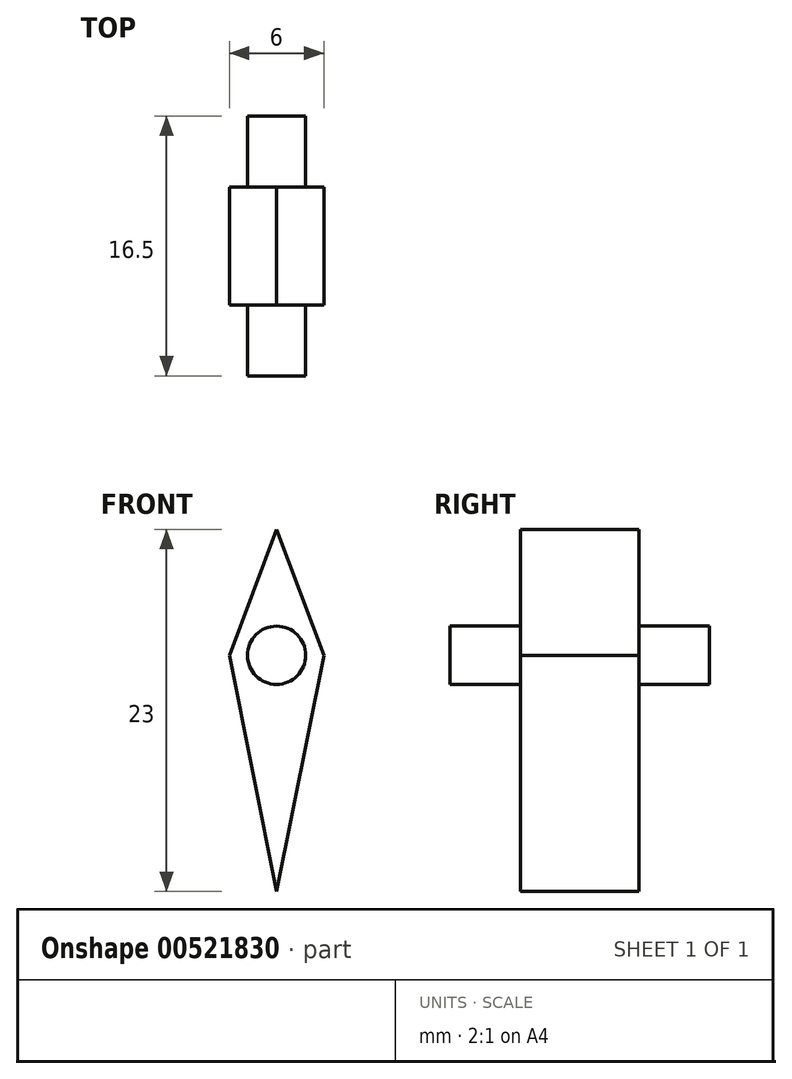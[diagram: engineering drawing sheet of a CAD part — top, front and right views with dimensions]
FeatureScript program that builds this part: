
annotation { "Feature Type Name" : "Feature", "Feature Type Description" : "" }
export const myFeature = defineFeature(function(context is Context, id is Id, definition is map)
    precondition{}
    {
        {
            var Q0;
            Q0=qCreatedBy(makeId("Front.planeOp"),FACE);
            var sketch = newSketch(context, id + "F0", { "sketchPlane" : qUnion([Q0])});
            skCircle(sketch, "E0", {"center": v(0, 0) * mm, "radius": 1.85 * mm});
            skLineSegment(sketch, "E1", {"start": v(0, 0) * mm, "end": v(0, 8) * mm});
            skLineSegment(sketch, "E2", {"start": v(0, 0) * mm, "end": v(0, -15) * mm});
            skLineSegment(sketch, "E3", {"start": v(0, 0) * mm, "end": v(-3, 0) * mm});
            skLineSegment(sketch, "E4", {"start": v(0, 0) * mm, "end": v(3, 0) * mm});
            skLineSegment(sketch, "E5", {"start": v(3, 0) * mm, "end": v(0, 8) * mm});
            skLineSegment(sketch, "E6", {"start": v(0, 8) * mm, "end": v(-3, 0) * mm});
            skLineSegment(sketch, "E7", {"start": v(0, -15) * mm, "end": v(-3, 0) * mm});
            skLineSegment(sketch, "E8", {"start": v(0, -15) * mm, "end": v(3, 0) * mm});
            skSolve(sketch);
        }
        {
            var Q0;
            {var subQ5=sQuery(id+"F0.wireOp",EDGE,"E8");Q0=makeQuery(id+"F0.imprint","IMPRINT",FACE,{"disambiguationData":[TD([[makeQuery(id+"F0.imprint","IMPRINT",EDGE,{"derivedFrom":subQ5}),1.0]])]});}
            var Q1;
            {var subQ5=sQuery(id+"F0.wireOp",EDGE,"E7");Q1=makeQuery(id+"F0.imprint","IMPRINT",FACE,{"disambiguationData":[TD([[makeQuery(id+"F0.imprint","IMPRINT",EDGE,{"derivedFrom":subQ5}),-1.0]])]});}
            var Q2;
            {var subQ0=sQuery(id+"F0.wireOp",EDGE,"E3");var subQ1=sQuery(id+"F0.wireOp",EDGE,"E0");var subQ2=makeQuery(id+"F0.imprint","INTERSECT",VERTEX,{"derivedFrom":[subQ1,subQ0]});Q2=makeQuery(id+"F0.imprint","IMPRINT",FACE,{"disambiguationData":[TD([[makeQuery(id+"F0.imprint","IMPRINT",EDGE,{"disambiguationData":[TD([[subQ2,-1.0]])],"derivedFrom":subQ1}),1.0]])]});}
            var Q3;
            {var subQ0=sQuery(id+"F0.wireOp",EDGE,"E2");var subQ1=sQuery(id+"F0.wireOp",EDGE,"E0");var subQ2=makeQuery(id+"F0.imprint","INTERSECT",VERTEX,{"derivedFrom":[subQ1,subQ0]});Q3=makeQuery(id+"F0.imprint","IMPRINT",FACE,{"disambiguationData":[TD([[makeQuery(id+"F0.imprint","IMPRINT",EDGE,{"disambiguationData":[TD([[subQ2,-1.0]])],"derivedFrom":subQ1}),1.0]])]});}
            var Q4;
            {var subQ0=sQuery(id+"F0.wireOp",EDGE,"E1");var subQ1=sQuery(id+"F0.wireOp",EDGE,"E0");var subQ2=makeQuery(id+"F0.imprint","INTERSECT",VERTEX,{"derivedFrom":[subQ1,subQ0]});Q4=makeQuery(id+"F0.imprint","IMPRINT",FACE,{"disambiguationData":[TD([[makeQuery(id+"F0.imprint","IMPRINT",EDGE,{"disambiguationData":[TD([[subQ2,1.0]])],"derivedFrom":subQ1}),1.0]])]});}
            var Q5;
            {var subQ0=sQuery(id+"F0.wireOp",EDGE,"E3");var subQ1=sQuery(id+"F0.wireOp",EDGE,"E0");var subQ2=makeQuery(id+"F0.imprint","INTERSECT",VERTEX,{"derivedFrom":[subQ1,subQ0]});Q5=makeQuery(id+"F0.imprint","IMPRINT",FACE,{"disambiguationData":[TD([[makeQuery(id+"F0.imprint","IMPRINT",EDGE,{"disambiguationData":[TD([[subQ2,1.0]])],"derivedFrom":subQ1}),1.0]])]});}
            var Q6;
            {var subQ5=sQuery(id+"F0.wireOp",EDGE,"E6");Q6=makeQuery(id+"F0.imprint","IMPRINT",FACE,{"disambiguationData":[TD([[makeQuery(id+"F0.imprint","IMPRINT",EDGE,{"derivedFrom":subQ5}),1.0]])]});}
            var Q7;
            {var subQ5=sQuery(id+"F0.wireOp",EDGE,"E5");Q7=makeQuery(id+"F0.imprint","IMPRINT",FACE,{"disambiguationData":[TD([[makeQuery(id+"F0.imprint","IMPRINT",EDGE,{"derivedFrom":subQ5}),1.0]])]});}
            extrude(context, id + "F1", {"entities" : qUnion([Q0, Q1, Q2, Q3, Q4, Q5, Q6, Q7]), "depth" : 7.5 * mm, "offsetDistance" : 25 * mm});
        }
        {
            var Q0;
            {var subQ0=sQuery(id+"F0.wireOp",EDGE,"E3");var subQ1=sQuery(id+"F0.wireOp",EDGE,"E0");var subQ2=makeQuery(id+"F0.imprint","INTERSECT",VERTEX,{"derivedFrom":[subQ1,subQ0]});Q0=makeQuery(id+"F0.imprint","IMPRINT",FACE,{"disambiguationData":[TD([[makeQuery(id+"F0.imprint","IMPRINT",EDGE,{"disambiguationData":[TD([[subQ2,-1.0]])],"derivedFrom":subQ1}),1.0]])]});}
            var Q1;
            {var subQ0=sQuery(id+"F0.wireOp",EDGE,"E3");var subQ1=sQuery(id+"F0.wireOp",EDGE,"E0");var subQ2=makeQuery(id+"F0.imprint","INTERSECT",VERTEX,{"derivedFrom":[subQ1,subQ0]});Q1=makeQuery(id+"F0.imprint","IMPRINT",FACE,{"disambiguationData":[TD([[makeQuery(id+"F0.imprint","IMPRINT",EDGE,{"disambiguationData":[TD([[subQ2,1.0]])],"derivedFrom":subQ1}),1.0]])]});}
            var Q2;
            {var subQ0=sQuery(id+"F0.wireOp",EDGE,"E1");var subQ1=sQuery(id+"F0.wireOp",EDGE,"E0");var subQ2=makeQuery(id+"F0.imprint","INTERSECT",VERTEX,{"derivedFrom":[subQ1,subQ0]});Q2=makeQuery(id+"F0.imprint","IMPRINT",FACE,{"disambiguationData":[TD([[makeQuery(id+"F0.imprint","IMPRINT",EDGE,{"disambiguationData":[TD([[subQ2,1.0]])],"derivedFrom":subQ1}),1.0]])]});}
            var Q3;
            {var subQ0=sQuery(id+"F0.wireOp",EDGE,"E2");var subQ1=sQuery(id+"F0.wireOp",EDGE,"E0");var subQ2=makeQuery(id+"F0.imprint","INTERSECT",VERTEX,{"derivedFrom":[subQ1,subQ0]});Q3=makeQuery(id+"F0.imprint","IMPRINT",FACE,{"disambiguationData":[TD([[makeQuery(id+"F0.imprint","IMPRINT",EDGE,{"disambiguationData":[TD([[subQ2,-1.0]])],"derivedFrom":subQ1}),1.0]])]});}
            extrude(context, id + "F2", {"entities" : qUnion([Q0, Q1, Q2, Q3]), "operationType" : NewBodyOperationType.ADD, "depth" : 12 * mm, "offsetDistance" : 25 * mm, "hasSecondDirection" : true, "secondDirectionOppositeDirection" : true, "secondDirectionDepth" : 4.5 * mm});
        }
    });
